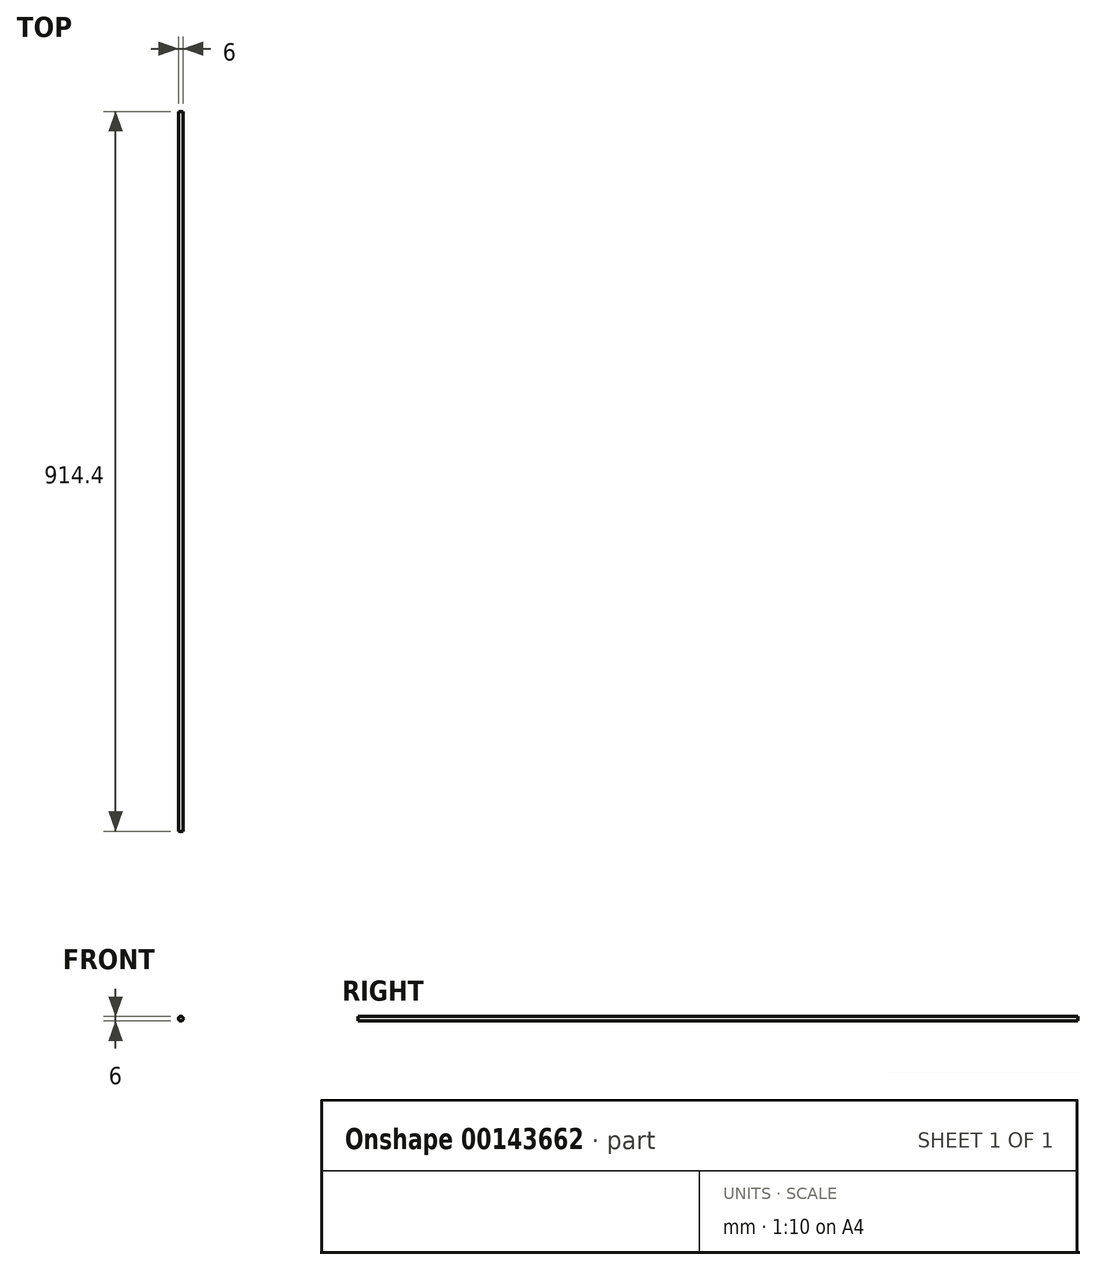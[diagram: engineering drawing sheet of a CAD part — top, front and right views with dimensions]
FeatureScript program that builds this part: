
annotation { "Feature Type Name" : "Feature", "Feature Type Description" : "" }
export const myFeature = defineFeature(function(context is Context, id is Id, definition is map)
    precondition{}
    {
        {
            var Q0;
            Q0=qCreatedBy(makeId("Front.planeOp"),FACE);
            var sketch = newSketch(context, id + "F0", { "sketchPlane" : qUnion([Q0])});
            skLineSegment(sketch, "E0", {"start": v(81.73, 9.93) * mm, "end": v(-150.94, 9.93) * mm, "construction": true});
            skCircle(sketch, "E1", {"center": v(-6.3, 40.42) * mm, "radius": 3 * mm});
            skSolve(sketch);
        }
        {
            var Q0;
            Q0=makeQuery(id+"F0.imprint","IMPRINT",FACE,{"disambiguationData":[TD([[makeQuery(id+"F0.imprint","IMPRINT",EDGE,{"derivedFrom":sQuery(id+"F0.wireOp",EDGE,"E1")}),1.0]])]});
            extrude(context, id + "F1", {"entities" : qUnion([Q0]), "depth" : 914.4 * mm});
        }
    });
